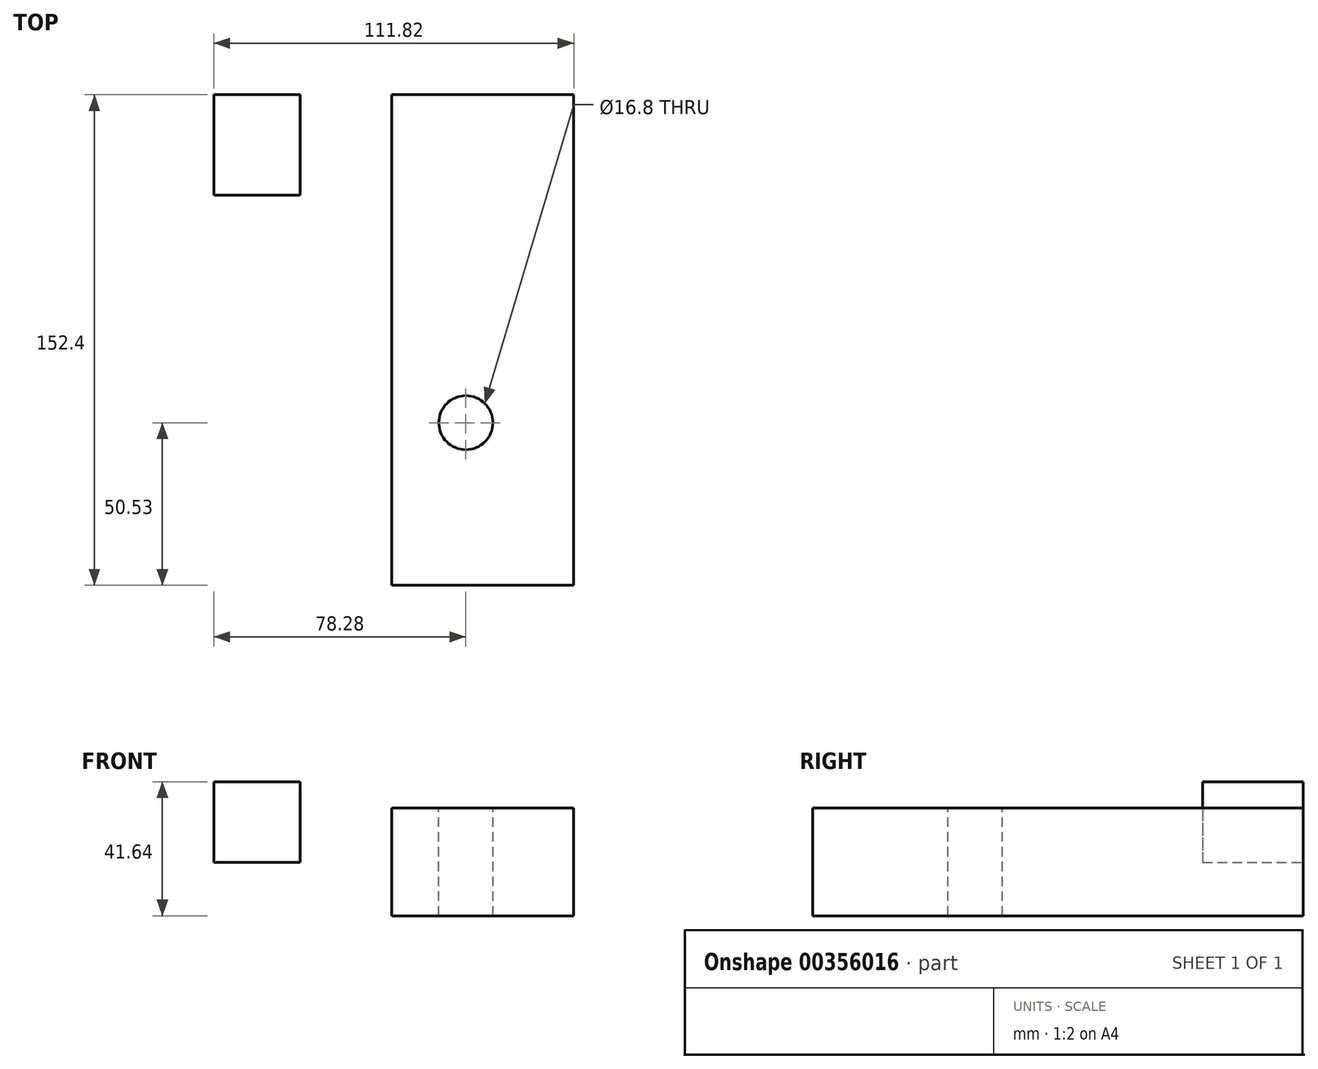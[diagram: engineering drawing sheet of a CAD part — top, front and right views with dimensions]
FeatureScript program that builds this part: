
annotation { "Feature Type Name" : "Feature", "Feature Type Description" : "" }
export const myFeature = defineFeature(function(context is Context, id is Id, definition is map)
    precondition{}
    {
        {
            var Q0;
            Q0=qCreatedBy(makeId("Front.planeOp"),FACE);
            var sketch = newSketch(context, id + "F0", { "sketchPlane" : qUnion([Q0])});
            skLineSegment(sketch, "E0.bottom", {"start": v(-22.97, 16.9) * mm, "end": v(33.54, 16.9) * mm});
            skLineSegment(sketch, "E0.top", {"start": v(-22.97, -16.64) * mm, "end": v(33.54, -16.64) * mm});
            skLineSegment(sketch, "E0.left", {"start": v(-22.97, 16.9) * mm, "end": v(-22.97, -16.64) * mm});
            skLineSegment(sketch, "E0.right", {"start": v(33.54, 16.9) * mm, "end": v(33.54, -16.64) * mm});
            skSolve(sketch);
        }
        {
            var Q0;
            Q0=makeQuery(id+"F0.imprint","IMPRINT",FACE,{"disambiguationData":[TD([[makeQuery(id+"F0.imprint","IMPRINT",EDGE,{"derivedFrom":sQuery(id+"F0.wireOp",EDGE,"E0.bottom")}),-1.0]])]});
            extrude(context, id + "F1", {"entities" : qUnion([Q0]), "depth" : 152.4 * mm});
        }
        {
            var Q0;
            Q0=makeQuery(id+"F1.opExtrude","SWEPT_FACE",FACE,{"disambiguationData":[OSD([sQuery(id+"F0.wireOp",EDGE,"E0.bottom")])]});
            var sketch = newSketch(context, id + "F2", { "sketchPlane" : qUnion([Q0])});
            skCircle(sketch, "E1", {"center": v(0, -101.87) * mm, "radius": 8.4 * mm});
            skSolve(sketch);
        }
        {
            var Q0;
            Q0=makeQuery(id+"F2.imprint","IMPRINT",FACE,{"disambiguationData":[TD([[makeQuery(id+"F2.imprint","IMPRINT",EDGE,{"derivedFrom":sQuery(id+"F2.wireOp",EDGE,"E1")}),1.0]])]});
            var Q1;
            Q1=sQuery(id+"F2.wireOp",EDGE,"E1");
            extrude(context, id + "F3", {"entities" : qUnion([Q0]), "operationType" : NewBodyOperationType.REMOVE, "surfaceEntities" : qUnion([Q1]), "oppositeDirection" : true, "depth" : 63.75 * mm});
        }
        {
            var Q0;
            Q0=qCreatedBy(makeId("Top.planeOp"),FACE);
            var sketch = newSketch(context, id + "F4", { "sketchPlane" : qUnion([Q0])});
            skLineSegment(sketch, "E2.bottom", {"start": v(-78.28, -31.17) * mm, "end": v(-51.53, -31.17) * mm});
            skLineSegment(sketch, "E2.top", {"start": v(-78.28, 0) * mm, "end": v(-51.53, 0) * mm});
            skLineSegment(sketch, "E2.left", {"start": v(-78.28, -31.17) * mm, "end": v(-78.28, 0) * mm});
            skLineSegment(sketch, "E2.right", {"start": v(-51.53, -31.17) * mm, "end": v(-51.53, 0) * mm});
            skSolve(sketch);
        }
        {
            var Q0;
            Q0=makeQuery(id+"F4.imprint","IMPRINT",FACE,{"disambiguationData":[TD([[makeQuery(id+"F4.imprint","IMPRINT",EDGE,{"derivedFrom":sQuery(id+"F4.wireOp",EDGE,"E2.bottom")}),1.0]])]});
            extrude(context, id + "F5", {"entities" : qUnion([Q0]), "depth" : 25 * mm});
        }
    });
